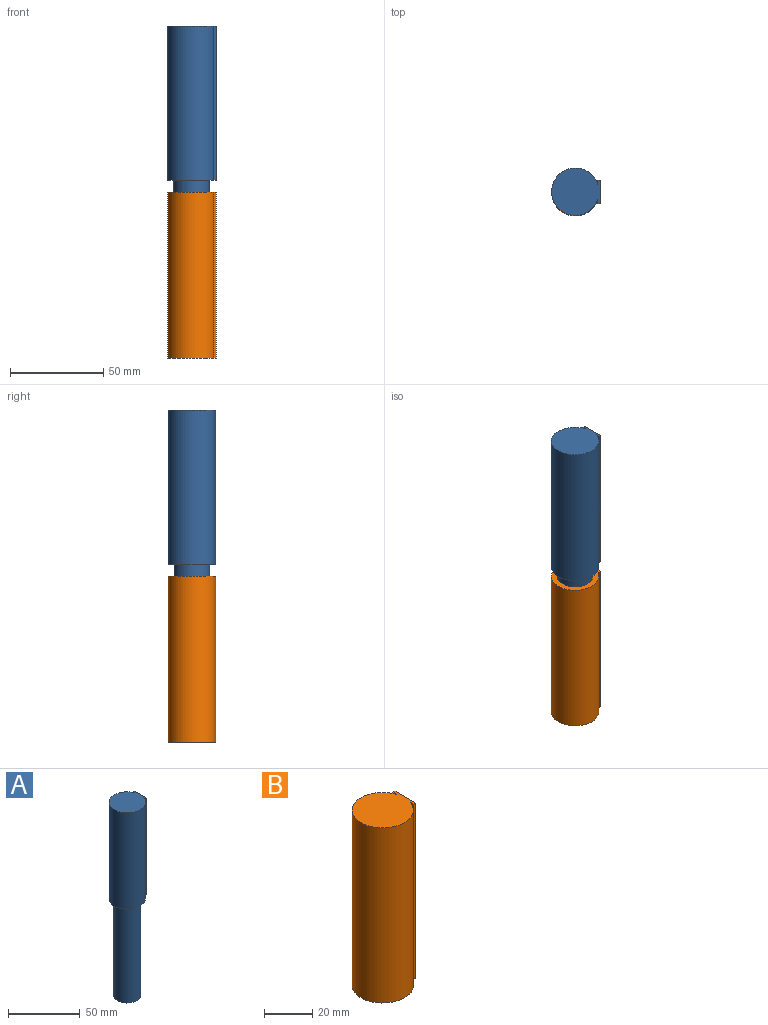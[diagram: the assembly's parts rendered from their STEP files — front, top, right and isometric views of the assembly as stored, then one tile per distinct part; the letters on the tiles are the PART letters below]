
ASSEMBLY  parts=2 mates=1
PART A: 10 faces, bbox 26x25.4x165.1 mm
  f0: plane 82.55x1.25mm, normal (0,-1,0), area 102.9mm2, adj f1,f5,f6,f8
  f1: plane 82.55x12.27mm, normal (1,0,0), area 1012.7mm2, adj f0,f2,f6,f8
  f2: plane 82.55x1.25mm, normal (0,1,0), area 102.9mm2, adj f1,f3,f6,f8
  f3: plane 82.55x2.2mm, normal (-1,0,0), area 182mm2, adj f2,f4,f6,f8
  f4: cylinder r=12.7mm len=82.55mm, axis (0,0,-1), area 5927.7mm2, adj f3,f5,f6,f8
  f5: plane 82.55x2.2mm, normal (-1,0,0), area 182mm2, adj f0,f4,f6,f8
  f6: plane 26.02x25.4mm, normal (0,0,1), area 518.7mm2, adj f0,f1,f2,f3,f4,f5
  f7: cylinder r=9.53mm len=82.55mm, axis (0,0,-1), area 4940.4mm2, adj f8,f9
  f8: plane 26.02x25.4mm, normal (0,0,-1), area 233.7mm2, adj f0,f1,f2,f3,f4,f5,f7
  f9: plane 19.05x19.05mm, normal (0,0,-1), area 285mm2, adj f7
PART B: 10 faces, bbox 26x25.4x88.9 mm
  f0: plane 88.9x1.25mm, normal (0,-1,0), area 110.8mm2, adj f1,f5,f6,f7
  f1: plane 88.9x12.27mm, normal (1,0,0), area 1090.6mm2, adj f0,f2,f6,f7
  f2: plane 88.9x1.25mm, normal (0,1,0), area 110.8mm2, adj f1,f3,f6,f7
  f3: plane 88.9x2.2mm, normal (-1,0,0), area 196mm2, adj f2,f4,f6,f7
  f4: cylinder r=12.7mm len=88.9mm, axis (0,0,-1), area 6383.6mm2, adj f3,f5,f6,f7
  f5: plane 88.9x2.2mm, normal (-1,0,0), area 196mm2, adj f0,f4,f6,f7
  f6: plane 26.02x25.4mm, normal (0,0,1), area 518.7mm2, adj f0,f1,f2,f3,f4,f5
  f7: plane 26.02x25.4mm, normal (0,0,-1), area 233.7mm2, adj f0,f1,f2,f3,f4,f5,f8
  f8: cylinder r=9.53mm len=76.2mm, axis (0,0,-1), area 4560.4mm2, adj f7,f9
  f9: plane 19.05x19.05mm, normal (0,0,-1), area 285mm2, adj f8
PLACE A t=(-10.38,15.48,-50.62)mm
PLACE B rot(axis=(1,0,0),180deg) t=(-10.38,15.48,25.58)mm
MATE revolute B.f8 <-> A.f7  axis (0,0,1) through (-10.38,15.48,-50.62)mm
